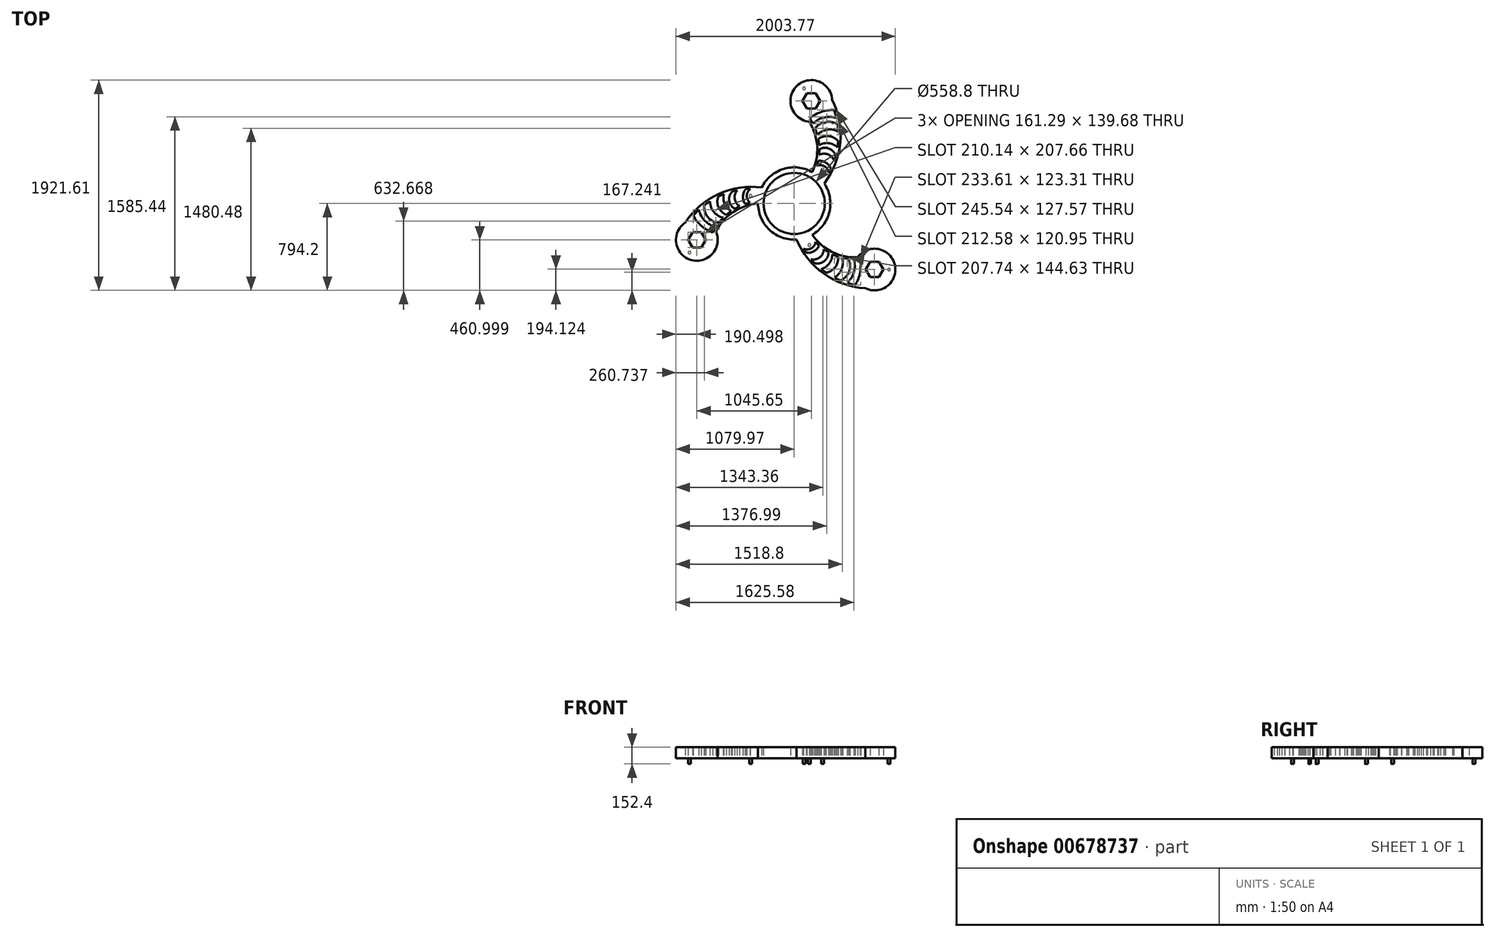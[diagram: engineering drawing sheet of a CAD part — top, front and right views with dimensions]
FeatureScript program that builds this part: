
annotation { "Feature Type Name" : "Feature", "Feature Type Description" : "" }
export const myFeature = defineFeature(function(context is Context, id is Id, definition is map)
    precondition{}
    {
        {
            var Q0;
            Q0=qCreatedBy(makeId("Top.planeOp"),FACE);
            var sketch = newSketch(context, id + "F0", { "sketchPlane" : qUnion([Q0])});
            skCircle(sketch, "E0", {"center": v(0, 0) * mm, "radius": 330.2 * mm});
            skArc(sketch, "E1", {"start": v(-295.98, 146.38) * mm, "mid": v(-691.32, 85.79) * mm, "end": v(-994.94, -174.56) * mm});
            skArc(sketch, "E2", {"start": v(-330.2, 0) * mm, "mid": v(-555.62, -78.09) * mm, "end": v(-715.84, -254.83) * mm});
            skArc(sketch, "E3", {"start": v(-818.87, -156.27) * mm, "mid": v(-998.12, -489.68) * mm, "end": v(-748.36, -205.22) * mm});
            skArc(sketch, "E4", {"start": v(-444.2, 130.87) * mm, "mid": v(-467.95, 63.66) * mm, "end": v(-447.52, -4.64) * mm});
            skLineSegment(sketch, "E5", {"start": v(-447.52, -4.64) * mm, "end": v(-403.07, 7.83) * mm});
            skLineSegment(sketch, "E6", {"start": v(-444.2, 130.87) * mm, "end": v(-399.74, 133.02) * mm});
            skArc(sketch, "E7", {"start": v(-399.74, 133.02) * mm, "mid": v(-432.98, 71.27) * mm, "end": v(-403.07, 7.83) * mm});
            skPoint(sketch, "E8.end.orphan", {"position": v(-453.15, 0) * mm});
            skLineSegment(sketch, "E9", {"start": v(-544.04, -48.42) * mm, "end": v(-498.32, -24.6) * mm});
            skLineSegment(sketch, "E10", {"start": v(-566.11, 110.29) * mm, "end": v(-520.4, 120.58) * mm});
            skArc(sketch, "E11", {"start": v(-520.4, 120.58) * mm, "mid": v(-542.84, 42.9) * mm, "end": v(-498.32, -24.6) * mm});
            skLineSegment(sketch, "E12", {"start": v(-620.12, -103.4) * mm, "end": v(-576.11, -68.97) * mm});
            skLineSegment(sketch, "E13", {"start": v(-693.63, 63.67) * mm, "end": v(-642.31, 85.79) * mm});
            skPoint(sketch, "E13.endSnap0", {"position": v(-691.32, 85.79) * mm});
            skArc(sketch, "E14", {"start": v(-693.63, 63.67) * mm, "mid": v(-690.53, -34.67) * mm, "end": v(-620.12, -103.4) * mm});
            skArc(sketch, "E15", {"start": v(-566.11, 110.29) * mm, "mid": v(-593.67, 25.57) * mm, "end": v(-544.04, -48.42) * mm});
            skArc(sketch, "E16", {"start": v(-642.31, 85.79) * mm, "mid": v(-634.72, -2.5) * mm, "end": v(-576.11, -68.97) * mm});
            skLineSegment(sketch, "E17", {"start": v(-821.71, -15.36) * mm, "end": v(-769.83, 21.24) * mm});
            skLineSegment(sketch, "E18", {"start": v(-689.25, -177.7) * mm, "end": v(-647.8, -129.6) * mm});
            skArc(sketch, "E19", {"start": v(-821.71, -15.36) * mm, "mid": v(-788.75, -123.68) * mm, "end": v(-689.25, -177.7) * mm});
            skArc(sketch, "E20", {"start": v(-769.83, 21.24) * mm, "mid": v(-735.26, -75.57) * mm, "end": v(-647.8, -129.6) * mm});
            skCircle(sketch, "E21.cCircle", {"center": v(-889.47, -333.2) * mm, "radius": 80.65 * mm, "construction": true});
            skLineSegment(sketch, "E21.0", {"start": v(-808.83, -333.2) * mm, "end": v(-849.15, -403.04) * mm});
            skLineSegment(sketch, "E21.1", {"start": v(-849.15, -403.04) * mm, "end": v(-929.8, -403.04) * mm});
            skLineSegment(sketch, "E21.2", {"start": v(-929.8, -403.04) * mm, "end": v(-970.12, -333.2) * mm});
            skLineSegment(sketch, "E21.3", {"start": v(-970.12, -333.2) * mm, "end": v(-929.8, -263.36) * mm});
            skLineSegment(sketch, "E21.4", {"start": v(-929.8, -263.36) * mm, "end": v(-849.15, -263.36) * mm});
            skLineSegment(sketch, "E21.5", {"start": v(-849.15, -263.36) * mm, "end": v(-808.83, -333.2) * mm});
            skLineSegment(sketch, "E22", {"start": v(-870.12, -56.46) * mm, "end": v(-923.06, -111.26) * mm});
            skLineSegment(sketch, "E23", {"start": v(-715.4, -215.8) * mm, "end": v(-743, -266.6) * mm});
            skArc(sketch, "E24", {"start": v(-870.12, -56.46) * mm, "mid": v(-816.29, -158.98) * mm, "end": v(-715.4, -215.8) * mm});
            skArc(sketch, "E25", {"start": v(-923.06, -111.26) * mm, "mid": v(-847.1, -205.24) * mm, "end": v(-743, -266.6) * mm});
            skArc(sketch, "E26.1.0", {"start": v(165.1, -285.96) * mm, "mid": v(345.43, -442.13) * mm, "end": v(578.6, -492.52) * mm});
            skArc(sketch, "E26.1.1", {"start": v(21.22, -329.52) * mm, "mid": v(271.37, -641.6) * mm, "end": v(648.64, -774.36) * mm});
            skArc(sketch, "E26.2.0", {"start": v(165.1, 285.96) * mm, "mid": v(210.18, 520.22) * mm, "end": v(137.23, 747.35) * mm});
            skArc(sketch, "E26.2.1", {"start": v(274.76, 183.14) * mm, "mid": v(419.96, 555.8) * mm, "end": v(346.3, 948.92) * mm});
            skLineSegment(sketch, "E27.1.0", {"start": v(813.94, -603.7) * mm, "end": v(773.62, -673.55) * mm});
            skLineSegment(sketch, "E27.1.1", {"start": v(692.97, -673.55) * mm, "end": v(652.65, -603.7) * mm});
            skLineSegment(sketch, "E27.1.2", {"start": v(773.62, -673.55) * mm, "end": v(692.97, -673.55) * mm});
            skLineSegment(sketch, "E27.2.0", {"start": v(115.85, 1006.75) * mm, "end": v(196.5, 1006.75) * mm});
            skLineSegment(sketch, "E27.2.1", {"start": v(236.82, 936.9) * mm, "end": v(196.5, 867.07) * mm});
            skLineSegment(sketch, "E27.2.2", {"start": v(196.5, 1006.75) * mm, "end": v(236.82, 936.9) * mm});
            skLineSegment(sketch, "E28.1.0", {"start": v(187.54, -545.4) * mm, "end": v(155.77, -510.96) * mm});
            skLineSegment(sketch, "E28.1.2", {"start": v(291.67, -632.53) * mm, "end": v(246.86, -599.15) * mm});
            skLineSegment(sketch, "E28.1.3", {"start": v(424.16, -703.94) * mm, "end": v(366.51, -677.31) * mm});
            skArc(sketch, "E28.1.4", {"start": v(544.77, -631.03) * mm, "mid": v(923.14, -619.56) * mm, "end": v(551.9, -545.49) * mm});
            skCircle(sketch, "E28.1.5", {"center": v(733.3, -603.7) * mm, "radius": 80.65 * mm, "construction": true});
            skLineSegment(sketch, "E28.1.6", {"start": v(399.62, -485.34) * mm, "end": v(347.8, -464.44) * mm});
            skArc(sketch, "E28.1.8", {"start": v(246.86, -599.15) * mm, "mid": v(319.53, -548.43) * mm, "end": v(347.8, -464.44) * mm});
            skLineSegment(sketch, "E28.1.10", {"start": v(483.96, -725.31) * mm, "end": v(557.89, -743.76) * mm});
            skArc(sketch, "E28.1.11", {"start": v(155.77, -510.96) * mm, "mid": v(234.26, -491.56) * mm, "end": v(270.46, -419.26) * mm});
            skLineSegment(sketch, "E28.1.12", {"start": v(108.76, -450.11) * mm, "end": v(84.67, -412.7) * mm});
            skArc(sketch, "E28.1.13", {"start": v(291.67, -632.53) * mm, "mid": v(375.3, -580.68) * mm, "end": v(399.62, -485.34) * mm});
            skArc(sketch, "E28.1.15", {"start": v(424.16, -703.94) * mm, "mid": v(501.48, -621.24) * mm, "end": v(498.52, -508.06) * mm});
            skArc(sketch, "E28.1.16", {"start": v(366.51, -677.31) * mm, "mid": v(433.08, -598.97) * mm, "end": v(436.13, -496.2) * mm});
            skLineSegment(sketch, "E28.1.17", {"start": v(227.78, -385.24) * mm, "end": v(194.75, -352.98) * mm});
            skArc(sketch, "E28.1.18", {"start": v(108.76, -450.11) * mm, "mid": v(178.85, -437.09) * mm, "end": v(227.78, -385.24) * mm});
            skArc(sketch, "E28.1.19", {"start": v(557.89, -743.76) * mm, "mid": v(601.29, -630.99) * mm, "end": v(602.38, -510.16) * mm});
            skLineSegment(sketch, "E28.1.20", {"start": v(773.62, -533.86) * mm, "end": v(813.94, -603.7) * mm});
            skLineSegment(sketch, "E28.1.21", {"start": v(498.52, -508.06) * mm, "end": v(436.13, -496.2) * mm});
            skArc(sketch, "E28.1.23", {"start": v(84.67, -412.7) * mm, "mid": v(154.77, -410.6) * mm, "end": v(194.75, -352.98) * mm});
            skLineSegment(sketch, "E28.1.24", {"start": v(313.95, -446.94) * mm, "end": v(270.46, -419.26) * mm});
            skArc(sketch, "E28.1.25", {"start": v(187.54, -545.4) * mm, "mid": v(274.7, -526.92) * mm, "end": v(313.95, -446.94) * mm});
            skLineSegment(sketch, "E28.1.26", {"start": v(544.6, -511.66) * mm, "end": v(602.38, -510.16) * mm});
            skLineSegment(sketch, "E28.1.27", {"start": v(652.65, -603.7) * mm, "end": v(692.97, -533.86) * mm});
            skLineSegment(sketch, "E28.1.28", {"start": v(692.97, -533.86) * mm, "end": v(773.62, -533.86) * mm});
            skArc(sketch, "E28.1.29", {"start": v(483.96, -725.31) * mm, "mid": v(545.82, -627.44) * mm, "end": v(544.6, -511.66) * mm});
            skLineSegment(sketch, "E28.2.0", {"start": v(378.57, 435.12) * mm, "end": v(364.62, 390.38) * mm});
            skLineSegment(sketch, "E28.2.2", {"start": v(401.95, 568.86) * mm, "end": v(395.45, 513.36) * mm});
            skLineSegment(sketch, "E28.2.3", {"start": v(397.55, 719.3) * mm, "end": v(403.31, 656.07) * mm});
            skArc(sketch, "E28.2.4", {"start": v(274.1, 787.3) * mm, "mid": v(74.98, 1109.24) * mm, "end": v(196.45, 750.71) * mm});
            skCircle(sketch, "E28.2.5", {"center": v(156.18, 936.9) * mm, "radius": 80.65 * mm, "construction": true});
            skLineSegment(sketch, "E28.2.6", {"start": v(220.5, 588.75) * mm, "end": v(228.32, 533.42) * mm});
            skArc(sketch, "E28.2.8", {"start": v(395.45, 513.36) * mm, "mid": v(315.2, 550.93) * mm, "end": v(228.32, 533.42) * mm});
            skLineSegment(sketch, "E28.2.10", {"start": v(386.16, 781.77) * mm, "end": v(365.17, 855.03) * mm});
            skArc(sketch, "E28.2.11", {"start": v(364.62, 390.38) * mm, "mid": v(308.58, 448.66) * mm, "end": v(227.86, 443.85) * mm});
            skLineSegment(sketch, "E28.2.12", {"start": v(335.43, 319.25) * mm, "end": v(315.07, 279.67) * mm});
            skArc(sketch, "E28.2.13", {"start": v(401.95, 568.86) * mm, "mid": v(315.23, 615.35) * mm, "end": v(220.5, 588.75) * mm});
            skArc(sketch, "E28.2.15", {"start": v(397.55, 719.3) * mm, "mid": v(287.27, 744.92) * mm, "end": v(190.73, 685.76) * mm});
            skArc(sketch, "E28.2.16", {"start": v(403.31, 656.07) * mm, "mid": v(302.18, 674.54) * mm, "end": v(211.66, 625.8) * mm});
            skLineSegment(sketch, "E28.2.17", {"start": v(219.74, 389.88) * mm, "end": v(208.32, 345.15) * mm});
            skArc(sketch, "E28.2.18", {"start": v(335.43, 319.25) * mm, "mid": v(289.1, 373.43) * mm, "end": v(219.74, 389.88) * mm});
            skArc(sketch, "E28.2.19", {"start": v(365.17, 855.03) * mm, "mid": v(245.8, 836.22) * mm, "end": v(140.62, 776.76) * mm});
            skLineSegment(sketch, "E28.2.20", {"start": v(75.53, 936.9) * mm, "end": v(115.85, 1006.75) * mm});
            skLineSegment(sketch, "E28.2.21", {"start": v(190.73, 685.76) * mm, "end": v(211.66, 625.8) * mm});
            skArc(sketch, "E28.2.23", {"start": v(315.07, 279.67) * mm, "mid": v(278.2, 339.34) * mm, "end": v(208.32, 345.15) * mm});
            skLineSegment(sketch, "E28.2.24", {"start": v(230.1, 495.36) * mm, "end": v(227.86, 443.85) * mm});
            skArc(sketch, "E28.2.25", {"start": v(378.57, 435.12) * mm, "mid": v(318.98, 501.35) * mm, "end": v(230.1, 495.36) * mm});
            skLineSegment(sketch, "E28.2.26", {"start": v(170.81, 727.46) * mm, "end": v(140.62, 776.76) * mm});
            skLineSegment(sketch, "E28.2.27", {"start": v(196.5, 867.07) * mm, "end": v(115.85, 867.07) * mm});
            skLineSegment(sketch, "E28.2.28", {"start": v(115.85, 867.07) * mm, "end": v(75.53, 936.9) * mm});
            skArc(sketch, "E28.2.29", {"start": v(386.16, 781.77) * mm, "mid": v(270.47, 786.42) * mm, "end": v(170.81, 727.46) * mm});
            skCircle(sketch, "E29", {"center": v(0, 0) * mm, "radius": 279.4 * mm});
            skSolve(sketch);
        }
        {
            var Q0;
            Q0 = qSketchRegion(id + "F0", true);
            extrude(context, id + "F1", {"entities" : qUnion([Q0]), "depth" : 101.6 * mm, "offsetDistance" : 25.4 * mm});
        }
        {
            var Q0;
            Q0=makeQuery(id+"F1.opExtrude","CAP_FACE",FACE,{"disambiguationData":[OSD([sQuery(id+"F0.wireOp",EDGE,"E0"),sQuery(id+"F0.wireOp",EDGE,"E1"),sQuery(id+"F0.wireOp",EDGE,"E2"),sQuery(id+"F0.wireOp",EDGE,"E3"),sQuery(id+"F0.wireOp",EDGE,"E4"),sQuery(id+"F0.wireOp",EDGE,"E5"),sQuery(id+"F0.wireOp",EDGE,"E6"),sQuery(id+"F0.wireOp",EDGE,"E7"),sQuery(id+"F0.wireOp",EDGE,"E9"),sQuery(id+"F0.wireOp",EDGE,"E10"),sQuery(id+"F0.wireOp",EDGE,"E11"),sQuery(id+"F0.wireOp",EDGE,"E12"),sQuery(id+"F0.wireOp",EDGE,"E13"),sQuery(id+"F0.wireOp",EDGE,"E14"),sQuery(id+"F0.wireOp",EDGE,"E15"),sQuery(id+"F0.wireOp",EDGE,"E16"),sQuery(id+"F0.wireOp",EDGE,"E17"),sQuery(id+"F0.wireOp",EDGE,"E18"),sQuery(id+"F0.wireOp",EDGE,"E19"),sQuery(id+"F0.wireOp",EDGE,"E20"),sQuery(id+"F0.wireOp",EDGE,"E21.0"),sQuery(id+"F0.wireOp",EDGE,"E21.1"),sQuery(id+"F0.wireOp",EDGE,"E21.2"),sQuery(id+"F0.wireOp",EDGE,"E21.3"),sQuery(id+"F0.wireOp",EDGE,"E21.4"),sQuery(id+"F0.wireOp",EDGE,"E21.5"),sQuery(id+"F0.wireOp",EDGE,"E22"),sQuery(id+"F0.wireOp",EDGE,"E23"),sQuery(id+"F0.wireOp",EDGE,"E24"),sQuery(id+"F0.wireOp",EDGE,"E25"),sQuery(id+"F0.wireOp",EDGE,"E28.1.0"),sQuery(id+"F0.wireOp",EDGE,"E26.1.0"),sQuery(id+"F0.wireOp",EDGE,"E28.1.2"),sQuery(id+"F0.wireOp",EDGE,"E28.1.3"),sQuery(id+"F0.wireOp",EDGE,"E28.1.4"),sQuery(id+"F0.wireOp",EDGE,"E28.1.6"),sQuery(id+"F0.wireOp",EDGE,"E27.1.0"),sQuery(id+"F0.wireOp",EDGE,"E28.1.8"),sQuery(id+"F0.wireOp",EDGE,"E27.1.1"),sQuery(id+"F0.wireOp",EDGE,"E28.1.10"),sQuery(id+"F0.wireOp",EDGE,"E28.1.11"),sQuery(id+"F0.wireOp",EDGE,"E28.1.12"),sQuery(id+"F0.wireOp",EDGE,"E28.1.13"),sQuery(id+"F0.wireOp",EDGE,"E26.1.1"),sQuery(id+"F0.wireOp",EDGE,"E28.1.15"),sQuery(id+"F0.wireOp",EDGE,"E28.1.16"),sQuery(id+"F0.wireOp",EDGE,"E28.1.17"),sQuery(id+"F0.wireOp",EDGE,"E28.1.18"),sQuery(id+"F0.wireOp",EDGE,"E28.1.19"),sQuery(id+"F0.wireOp",EDGE,"E28.1.20"),sQuery(id+"F0.wireOp",EDGE,"E28.1.21"),sQuery(id+"F0.wireOp",EDGE,"E27.1.2"),sQuery(id+"F0.wireOp",EDGE,"E28.1.23"),sQuery(id+"F0.wireOp",EDGE,"E28.1.24"),sQuery(id+"F0.wireOp",EDGE,"E28.1.25"),sQuery(id+"F0.wireOp",EDGE,"E28.1.26"),sQuery(id+"F0.wireOp",EDGE,"E28.1.27"),sQuery(id+"F0.wireOp",EDGE,"E28.1.28"),sQuery(id+"F0.wireOp",EDGE,"E28.1.29"),sQuery(id+"F0.wireOp",EDGE,"E28.2.0"),sQuery(id+"F0.wireOp",EDGE,"E26.2.0"),sQuery(id+"F0.wireOp",EDGE,"E28.2.2"),sQuery(id+"F0.wireOp",EDGE,"E28.2.3"),sQuery(id+"F0.wireOp",EDGE,"E28.2.4"),sQuery(id+"F0.wireOp",EDGE,"E28.2.6"),sQuery(id+"F0.wireOp",EDGE,"E27.2.0"),sQuery(id+"F0.wireOp",EDGE,"E28.2.8"),sQuery(id+"F0.wireOp",EDGE,"E27.2.1"),sQuery(id+"F0.wireOp",EDGE,"E28.2.10"),sQuery(id+"F0.wireOp",EDGE,"E28.2.11"),sQuery(id+"F0.wireOp",EDGE,"E28.2.12"),sQuery(id+"F0.wireOp",EDGE,"E28.2.13"),sQuery(id+"F0.wireOp",EDGE,"E26.2.1"),sQuery(id+"F0.wireOp",EDGE,"E28.2.15"),sQuery(id+"F0.wireOp",EDGE,"E28.2.16"),sQuery(id+"F0.wireOp",EDGE,"E28.2.17"),sQuery(id+"F0.wireOp",EDGE,"E28.2.18"),sQuery(id+"F0.wireOp",EDGE,"E28.2.19"),sQuery(id+"F0.wireOp",EDGE,"E28.2.20"),sQuery(id+"F0.wireOp",EDGE,"E28.2.21"),sQuery(id+"F0.wireOp",EDGE,"E27.2.2"),sQuery(id+"F0.wireOp",EDGE,"E28.2.23"),sQuery(id+"F0.wireOp",EDGE,"E28.2.24"),sQuery(id+"F0.wireOp",EDGE,"E28.2.25"),sQuery(id+"F0.wireOp",EDGE,"E28.2.26"),sQuery(id+"F0.wireOp",EDGE,"E28.2.27"),sQuery(id+"F0.wireOp",EDGE,"E28.2.28"),sQuery(id+"F0.wireOp",EDGE,"E28.2.29"),sQuery(id+"F0.wireOp",EDGE,"E29")])],"isStart":true});
            var sketch = newSketch(context, id + "F2", { "sketchPlane" : qUnion([Q0])});
            skPoint(sketch, "E30.center.orphan", {"position": v(237.5, -272.97) * mm});
            skCircle(sketch, "E31.1.0", {"center": v(138.18, 380.01) * mm, "radius": 12.7 * mm});
            skPoint(sketch, "E31.center", {"position": v(-4.7, 5.95) * mm});
            skCircle(sketch, "E32", {"center": v(866.3, 604.33) * mm, "radius": 12.5 * mm});
            skCircle(sketch, "E33.1.0", {"center": v(-956.51, 448.07) * mm, "radius": 12.5 * mm});
            skCircle(sketch, "E33.2.0", {"center": v(90.22, -1052.4) * mm, "radius": 12.5 * mm});
            skPoint(sketch, "E33.center", {"position": v(0, 0) * mm});
            skCircle(sketch, "E34.1.0", {"center": v(-398.2, -70.34) * mm, "radius": 12.7 * mm});
            skCircle(sketch, "E34.2.0", {"center": v(260.01, -309.67) * mm, "radius": 12.7 * mm});
            skSolve(sketch);
        }
        {
            var Q0;
            Q0 = qSketchRegion(id + "F2", true);
            extrude(context, id + "F3", {"entities" : qUnion([Q0]), "operationType" : NewBodyOperationType.ADD, "depth" : 50.8 * mm, "offsetDistance" : 25.4 * mm});
        }
    });
